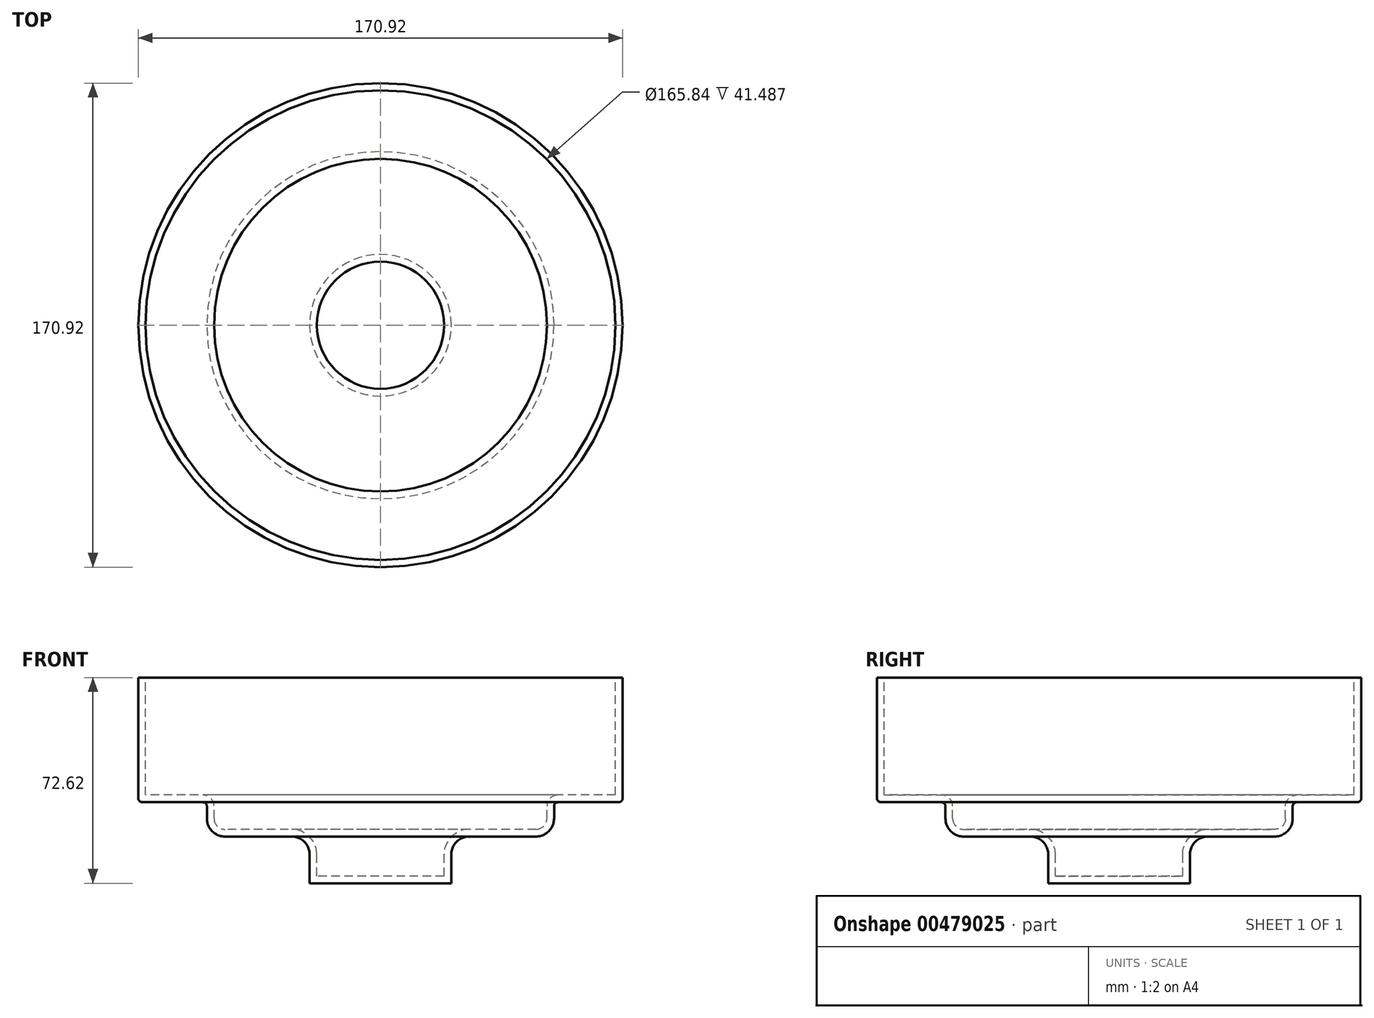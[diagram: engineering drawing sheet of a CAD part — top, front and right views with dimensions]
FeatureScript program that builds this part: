
annotation { "Feature Type Name" : "Feature", "Feature Type Description" : "" }
export const myFeature = defineFeature(function(context is Context, id is Id, definition is map)
    precondition{}
    {
        {
            var Q0;
            Q0=qCreatedBy(makeId("Front.planeOp"),FACE);
            var sketch = newSketch(context, id + "F0", { "sketchPlane" : qUnion([Q0])});
            skLineSegment(sketch, "E0", {"start": v(0, 0) * mm, "end": v(25, 0) * mm});
            skLineSegment(sketch, "E1", {"start": v(25, 0) * mm, "end": v(25, 10.15) * mm});
            skLineSegment(sketch, "E2", {"start": v(31.35, 16.5) * mm, "end": v(54.93, 16.5) * mm});
            skLineSegment(sketch, "E3", {"start": v(61.28, 22.85) * mm, "end": v(61.28, 27.2) * mm});
            skLineSegment(sketch, "E4", {"start": v(62.66, 28.6) * mm, "end": v(84.07, 28.6) * mm});
            skLineSegment(sketch, "E5", {"start": v(85.46, 29.98) * mm, "end": v(85.46, 72.62) * mm});
            skLineSegment(sketch, "E6", {"start": v(85.46, 72.62) * mm, "end": v(0, 72.62) * mm});
            skLineSegment(sketch, "E7", {"start": v(0, 72.62) * mm, "end": v(0, 0) * mm, "construction": true});
            skPoint(sketch, "E8.visualSharp", {"position": v(25, 16.5) * mm});
            skArc(sketch, "E8.filletArc", {"start": v(31.35, 16.5) * mm, "mid": v(26.86, 14.64) * mm, "end": v(25, 10.15) * mm});
            skPoint(sketch, "E9.visualSharp", {"position": v(61.28, 16.5) * mm});
            skArc(sketch, "E9.filletArc", {"start": v(54.93, 16.5) * mm, "mid": v(59.42, 18.36) * mm, "end": v(61.28, 22.85) * mm});
            skPoint(sketch, "E10.visualSharp", {"position": v(61.28, 28.6) * mm});
            skArc(sketch, "E10.filletArc", {"start": v(62.66, 28.6) * mm, "mid": v(61.68, 28.19) * mm, "end": v(61.28, 27.2) * mm});
            skPoint(sketch, "E11.visualSharp", {"position": v(85.46, 28.6) * mm});
            skArc(sketch, "E11.filletArc", {"start": v(84.07, 28.6) * mm, "mid": v(85.05, 29) * mm, "end": v(85.46, 29.98) * mm});
            skLineSegment(sketch, "E12", {"start": v(0, 72.62) * mm, "end": v(0, 0) * mm});
            skSolve(sketch);
        }
        {
            var Q0;
            Q0=qSketchRegion(id+"F0",true);
            var Q1;
            Q1=sQuery(id+"F0.wireOp",EDGE,"E12");
            revolve(context, id + "F1", {"entities" : qUnion([Q0]), "axis" : qUnion([Q1]), "revolveType" : RevolveType.FULL});
        }
        {
            var Q0;
            Q0=makeQuery(id+"F1.opRevolve","SWEPT_FACE",FACE,{"disambiguationData":[OSD([sQuery(id+"F0.wireOp",EDGE,"E6")])]});
            shell(context, id + "F2", {"entities" : qUnion([Q0]), "thickness" : 2.54 * mm});
        }
    });
